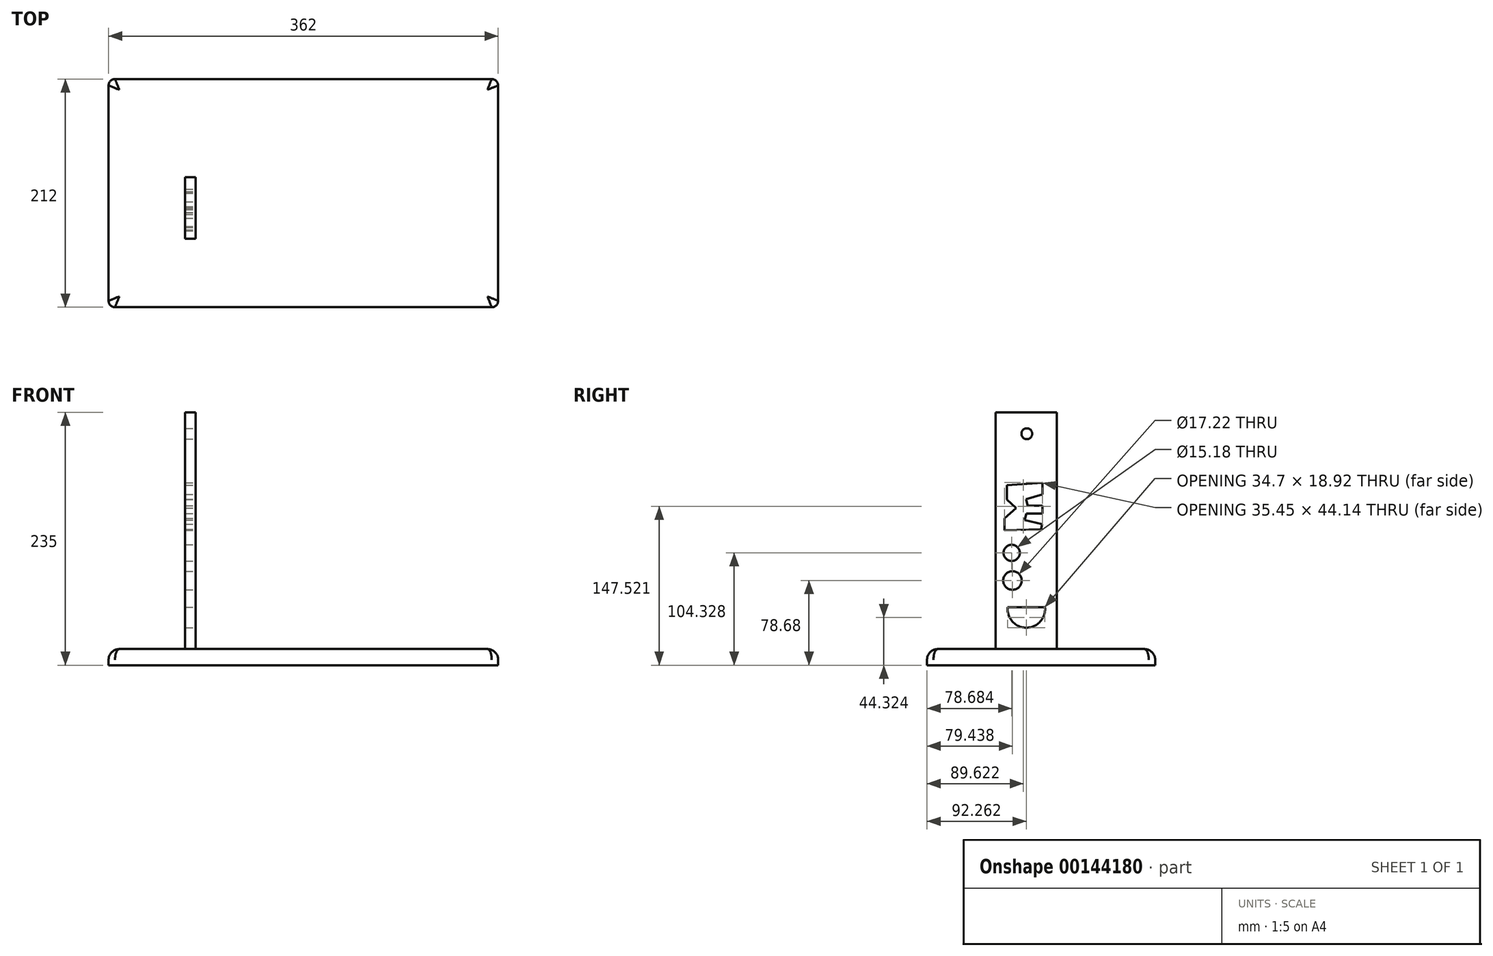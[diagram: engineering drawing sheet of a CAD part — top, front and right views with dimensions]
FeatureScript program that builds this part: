
annotation { "Feature Type Name" : "Feature", "Feature Type Description" : "" }
export const myFeature = defineFeature(function(context is Context, id is Id, definition is map)
    precondition{}
    {
        {
            var Q0;
            Q0=qCreatedBy(makeId("Top.planeOp"),FACE);
            var sketch = newSketch(context, id + "F0", { "sketchPlane" : qUnion([Q0])});
            skLineSegment(sketch, "E0.bottom", {"start": v(-6, 0) * mm, "end": v(-356, 0) * mm});
            skLineSegment(sketch, "E0.top", {"start": v(-6, 212) * mm, "end": v(-356, 212) * mm});
            skLineSegment(sketch, "E0.left", {"start": v(0, 6) * mm, "end": v(0, 206) * mm});
            skLineSegment(sketch, "E0.right", {"start": v(-362, 6) * mm, "end": v(-362, 206) * mm});
            skPoint(sketch, "E1.visualSharp", {"position": v(-362, 212) * mm});
            skArc(sketch, "E1.filletArc", {"start": v(-356, 212) * mm, "mid": v(-360.24, 210.24) * mm, "end": v(-362, 206) * mm});
            skPoint(sketch, "E2.visualSharp", {"position": v(-362, 0) * mm});
            skArc(sketch, "E2.filletArc", {"start": v(-362, 6) * mm, "mid": v(-360.24, 1.76) * mm, "end": v(-356, 0) * mm});
            skPoint(sketch, "E3.visualSharp", {"position": v(0, 212) * mm});
            skArc(sketch, "E3.filletArc", {"start": v(0, 206) * mm, "mid": v(-1.76, 210.24) * mm, "end": v(-6, 212) * mm});
            skPoint(sketch, "E4.visualSharp", {"position": v(0, 0) * mm});
            skArc(sketch, "E4.filletArc", {"start": v(-6, 0) * mm, "mid": v(-1.76, 1.76) * mm, "end": v(0, 6) * mm});
            skSolve(sketch);
        }
        {
            var Q0;
            Q0=makeQuery(id+"F0.imprint","IMPRINT",FACE,{"disambiguationData":[TD([[makeQuery(id+"F0.imprint","IMPRINT",EDGE,{"derivedFrom":sQuery(id+"F0.wireOp",EDGE,"E0.bottom")}),-1.0]])]});
            extrude(context, id + "F1", {"entities" : qUnion([Q0]), "depth" : 15 * mm});
        }
        {
            var Q0;
            Q0=qCreatedBy(makeId("Front.planeOp"),FACE);
            var sketch = newSketch(context, id + "F2", { "sketchPlane" : qUnion([Q0])});
            skLineSegment(sketch, "E5.0", {"start": v(-6, 15) * mm, "end": v(-356, 15) * mm});
            skLineSegment(sketch, "E6.bottom", {"start": v(-291, 15) * mm, "end": v(-281, 15) * mm});
            skLineSegment(sketch, "E6.top", {"start": v(-291, 235) * mm, "end": v(-281, 235) * mm});
            skLineSegment(sketch, "E6.left", {"start": v(-291, 15) * mm, "end": v(-291, 235) * mm});
            skLineSegment(sketch, "E6.right", {"start": v(-281, 15) * mm, "end": v(-281, 235) * mm});
            skSolve(sketch);
        }
        {
            var Q0;
            Q0 = qSketchRegion(id + "F2", true);
            extrude(context, id + "F3", {"entities" : qUnion([Q0]), "operationType" : NewBodyOperationType.ADD, "oppositeDirection" : true, "depth" : (77 + 43.7) * mm, "hasSecondDirection" : true, "secondDirectionOppositeDirection" : true, "secondDirectionDepth" : (20 + 43.7) * mm});
        }
        {
            var Q0;
            Q0=qCreatedBy(makeId("Right.planeOp"),FACE);
            var sketch = newSketch(context, id + "F4", { "sketchPlane" : qUnion([Q0])});
            skCircle(sketch, "E7", {"center": v(92.78, 215) * mm, "radius": 5 * mm});
            skLineSegment(sketch, "E8", {"start": v(107.35, 169.6) * mm, "end": v(107.35, 158.55) * mm});
            skLineSegment(sketch, "E9", {"start": v(107.35, 169.6) * mm, "end": v(74.16, 167.32) * mm});
            skLineSegment(sketch, "E10", {"start": v(74.16, 167.32) * mm, "end": v(74.16, 154.04) * mm});
            skLineSegment(sketch, "E11", {"start": v(74.16, 154.04) * mm, "end": v(82.83, 145.82) * mm});
            skLineSegment(sketch, "E12", {"start": v(82.83, 145.82) * mm, "end": v(71.9, 136.39) * mm});
            skLineSegment(sketch, "E13", {"start": v(71.9, 136.39) * mm, "end": v(71.9, 125.45) * mm});
            skLineSegment(sketch, "E14", {"start": v(71.9, 125.45) * mm, "end": v(105.83, 126.3) * mm});
            skLineSegment(sketch, "E15", {"start": v(105.83, 126.3) * mm, "end": v(106.96, 131.03) * mm});
            skLineSegment(sketch, "E16", {"start": v(106.96, 131.03) * mm, "end": v(90.75, 134.88) * mm});
            skLineSegment(sketch, "E17", {"start": v(91.88, 154.28) * mm, "end": v(107.35, 158.55) * mm});
            skCircle(sketch, "E18", {"center": v(78.68, 104.33) * mm, "radius": 7.6 * mm});
            skCircle(sketch, "E19", {"center": v(79.44, 78.68) * mm, "radius": 8.6 * mm});
            skLineSegment(sketch, "E20", {"start": v(74.91, 53.79) * mm, "end": v(109.61, 53.79) * mm});
            skArc(sketch, "E21", {"start": v(74.91, 53.79) * mm, "mid": v(92.26, 34.86) * mm, "end": v(109.61, 53.79) * mm});
            skLineSegment(sketch, "E22", {"start": v(91.88, 154.28) * mm, "end": v(93.6, 148.07) * mm});
            skLineSegment(sketch, "E23", {"start": v(93.6, 148.07) * mm, "end": v(107.35, 148.07) * mm});
            skLineSegment(sketch, "E24", {"start": v(107.35, 148.07) * mm, "end": v(107.35, 140.91) * mm});
            skLineSegment(sketch, "E25", {"start": v(107.35, 140.91) * mm, "end": v(92.26, 140.91) * mm});
            skLineSegment(sketch, "E26", {"start": v(90.75, 134.88) * mm, "end": v(92.26, 140.91) * mm});
            skSolve(sketch);
        }
        {
            var Q0;
            Q0=makeQuery(id+"F1.opExtrude","CAP_EDGE",EDGE,{"disambiguationData":[OSD([sQuery(id+"F0.wireOp",EDGE,"E0.bottom")])],"isStart":false});
            var Q1;
            Q1=makeQuery(id+"F1.opExtrude","CAP_EDGE",EDGE,{"disambiguationData":[OSD([sQuery(id+"F0.wireOp",EDGE,"E0.left")])],"isStart":false});
            fillet(context, id + "F5", {"entities" : qUnion([Q0, Q1]), "radius" : 10 * mm, "tangentPropagation" : true, "allowEdgeOverflow" : false});
        }
        {
            var Q0;
            Q0 = qSketchRegion(id + "F4", true);
            extrude(context, id + "F6", {"entities" : qUnion([Q0]), "operationType" : NewBodyOperationType.REMOVE, "oppositeDirection" : true, "depth" : 500000 * mm});
        }
    });
